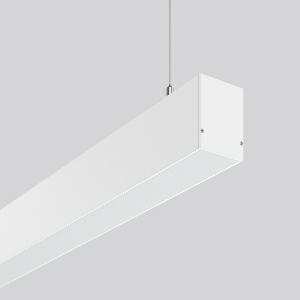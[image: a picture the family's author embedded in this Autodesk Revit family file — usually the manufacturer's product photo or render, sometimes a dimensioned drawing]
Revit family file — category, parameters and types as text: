
# Revit family: less_is_more_50_312319_002_1_7ad6
name_source: partatom
category: Lighting Fixtures
units: mm (PartAtom-declared; Revit-internal decimal feet)

## family parameters
Cut with Voids When Loaded = No
Host = Face
Light Source = No
Part Type = Normal
Room Calculation Point = No
Round Connector Dimension = Use Diameter
Shared = No

## types (1)
- LESS IS MORE 50 (1 x LED Modul 840, 6450 lm, 4000)
    Apparent Load = 52 VA
    CIE Flux Codes = 49 80 96 63 100
    Color Rendering = 80
    Color Temperature = 4000
    Default Elevation = 1800 mm
    Description = Series: LESS IS MORE 50
Linear pendant luminaire for aesthetically sophisticated lighting. Housing: extruded aluminium profile, powder-coated. End cap aluminium powder-coated. Canopy made of aluminium, powder-coated. Diffuser made of non-yellowing plastic (PMMA), opal. Direct 65%, indirect 35% light emission. Suitable for pendant. 2-point steel cable suspension freely positionable and infinitely height-adjustable. Special lengths available on request. LED unit with integrated converter interchangeable and removable. Suitable for through-wiring. With sensors or as a safety luminaire on request. 
Colour: traffic white, matt (RAL 9016)
Length: 1407 mm
Width: 57 mm
Height: 75 mm
Suspension length: 2000 mm
Lamp: LED
Socket: without socket
Colour temperature: 4000K
Colour rendering index (CRI): 80
Light source: LED
Socket lamp2: Without base
Colour temperature: 4000K
System power: 52 W
Rated luminous flux: 6450 lm
Luminous efficiency: 124 lm/W
Control gear: Regulated power supply
Control gear: Regulated power supply
Protection class: I
Type of protection: IP 20
    Height = 75 mm
    Lamp = 1 x LED Modul 840
    Lamp Light Flux = 6450 lm
    Lamp count = 1
    Length = 1407 mm
    Lifetime = 50000 h
    Luminous efficacy = 124 lm/W
    Manufacturer = RZB
    ModVariant = No
    Model = 312319.002.1
    Mounting Place = Ceiling
    Mounting Type = Pendant
    Number of Poles = 1
    OnlyDefault = Yes
    Power Factor = 1
    Product Name = LESS IS MORE 50
    Product group = Pendant LED linear luminaires
    ProductGroupID = 907
    Protection Class = Protection class I
    Protection Degree = IP 20
    RLX_Detail_Level = 1
    RLX_Emergency_Light_Flux = 0 lm
    RLX_Emergency_Type = 0
    RLX_Emergency_Type_DB = No
    RlxData = <blob elided: 31593 chars, md5=b6bbd21d>
    Socket = socket
    Standby Power = 0 W
    System Light Flux = 6450 lm
    System Power = 52 W
    Type Comments = Product without accessories
    Type Image = 312318.002.jpg
    URL = http://relux.com
    VarID = ---
    Voltage = 230 V
    Voltage Range = 220-240 V
    Weight = 0.00 kg
    Width = 57 mm

## geometry (parser evidence)
native form markers: Blend x4, Sweep x11
no freeform markers — native parametric forms only
